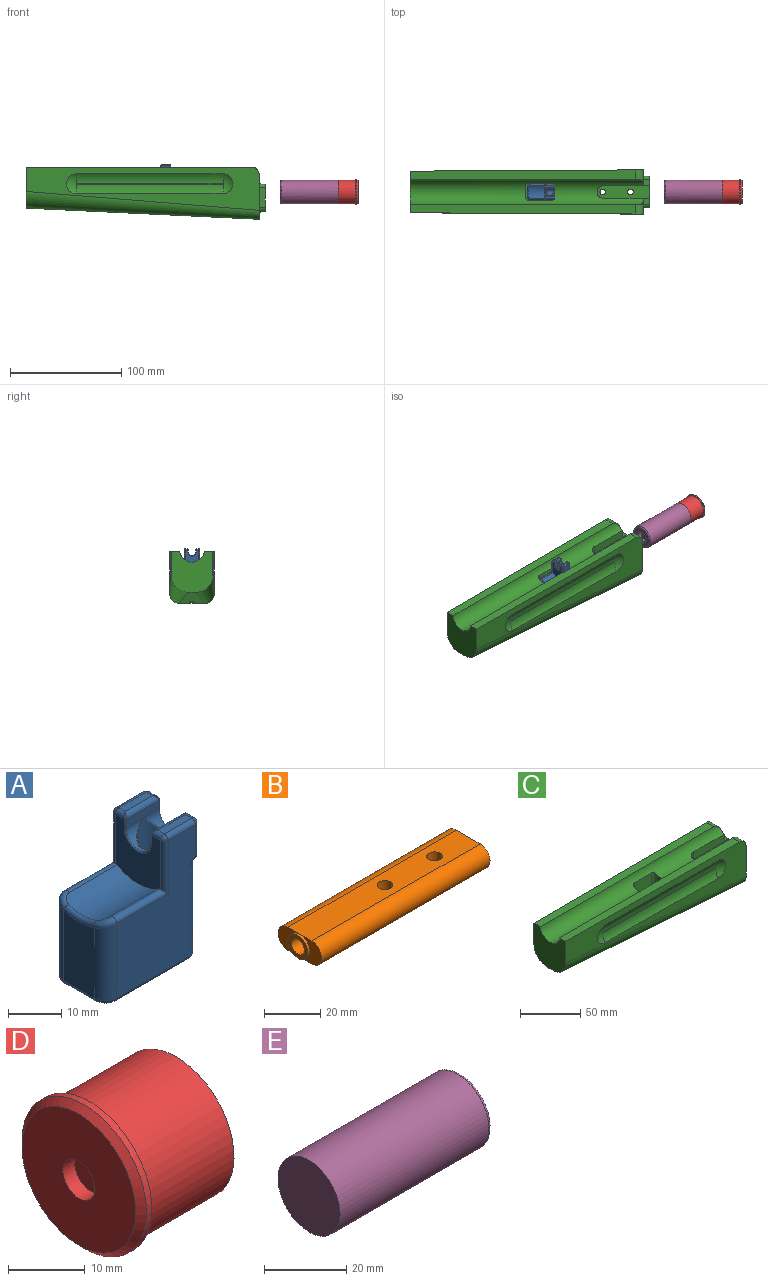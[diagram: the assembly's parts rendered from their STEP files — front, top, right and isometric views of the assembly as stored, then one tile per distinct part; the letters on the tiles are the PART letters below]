
ASSEMBLY  parts=5 mates=4
PART A: 77 faces, bbox 26.7x15.8x31.6 mm
  f0: plane 1.55x0.92mm, normal (1,0,0), area 0.6mm2, adj f1,f75,f76
  f1: cylinder r=6.5mm len=12.57mm, axis (1,0,0), area 12.9mm2, adj f0,f2,f3,f74,f75,f76
  f2: plane 1.55x0.92mm, normal (1,0,0), area 0.6mm2, adj f1,f3,f75
  f3: cylinder r=3mm len=21.61mm, axis (0,0,-1), area 83.5mm2, adj f1,f2,f4,f5,f69,f70,f71,f72
  f4: cylinder r=6.5mm len=12.57mm, axis (1,0,0), area 12.9mm2, adj f3,f5,f74,f76
  f5: plane 18.42x12.1mm, normal (1,0,0), area 136.6mm2, adj f3,f4,f6,f60,f61,f62,f63,f64
  f6: bspline ~2.27x1.53mm, area 0.7mm2, adj f5,f7,f60
  f7: torus R=4mm, axis (0,0,-1), area 2.1mm2, adj f6,f8,f59,f76
  f8: bspline ~2.77x1.82mm, area 0.7mm2, adj f7,f9,f11
  f9: bspline ~1.4x1.29mm, area 0.5mm2, adj f8,f10,f11,f59
  f10: sphere r=1mm, area 0.6mm2, adj f9,f60,f61
  f11: plane 29.5x21mm, normal (0,-1,0), area 407.5mm2, adj f8,f9,f12,f54,f55,f56,f57,f61
  f12: cylinder r=1mm len=19mm, axis (-1,0,0), area 29.8mm2, adj f11,f13,f14,f53
  f13: torus R=2mm, axis (0,0,-1), area 6.5mm2, adj f12,f14,f75,f76
  f14: plane 23x12.1mm, normal (0,0,-1), area 274.9mm2, adj f12,f13,f15,f51,f52,f53,f73,f75
  f15: cylinder r=1mm len=8.1mm, axis (0,1,0), area 12.7mm2, adj f14,f16,f52,f53
  f16: plane 16.26x8.1mm, normal (-1,0,0), area 127.8mm2, adj f15,f17,f50,f54
  f17: cylinder r=3mm len=17.19mm, axis (0,0,-1), area 78.8mm2, adj f16,f18,f52,f72
  f18: bspline ~3.94x3.84mm, area 8.1mm2, adj f17,f19,f48,f50
  f19: cylinder r=1mm len=13.7mm, axis (-1,0,0), area 27.5mm2, adj f18,f20,f47,f48,f72
  f20: cylinder r=1mm len=12.31mm, axis (0,0,-1), area 18.5mm2, adj f19,f21,f47,f72
  f21: sphere r=1mm, area 2.1mm2, adj f20,f22,f45
  f22: cylinder r=1mm len=2.4mm, axis (0,1,0), area 3.2mm2, adj f21,f23,f44,f47
  f23: plane 7.3x1.7mm, normal (0,0,1), area 12.4mm2, adj f22,f24,f45,f66
  f24: cylinder r=1mm len=8.7mm, axis (-1,0,0), area 12.6mm2, adj f23,f25,f43,f44
  f25: plane 8.7x2mm, normal (0,-1,0), area 17.4mm2, adj f24,f26,f41,f42,f65
  f26: cylinder r=3.35mm len=6.7mm, axis (-1,0,0), area 21.3mm2, adj f25,f27,f32,f64
  f27: bspline ~6.7x3.65mm, area 0.6mm2, adj f26,f28
  f28: cylinder r=3.35mm len=16.85mm, axis (0,0,1), area 305.8mm2, adj f27,f29,f30,f31
  f29: bspline ~5.8x3.65mm, area 1.2mm2, adj f28,f41
  f30: bspline ~2.9x2.9mm, area 0.1mm2, adj f28,f41
  f31: torus R=4.65mm, axis (0,1,0), area 132mm2, adj f28,f74
  f32: plane 8.7x2mm, normal (0,1,0), area 17.4mm2, adj f26,f33,f39,f41,f63
  f33: cylinder r=1mm len=8.7mm, axis (-1,0,0), area 12.6mm2, adj f32,f34,f37,f38
  f34: plane 7.3x1.7mm, normal (0,0,1), area 12.4mm2, adj f33,f35,f57,f62
  f35: cylinder r=1mm len=2.4mm, axis (0,1,0), area 3.2mm2, adj f34,f36,f37,f47
  f36: sphere r=1mm, area 1.6mm2, adj f35,f56,f57
  f37: bspline ~1.17x1mm, area 0.3mm2, adj f33,f35,f39
  f38: bspline ~1.04x1mm, area 0.3mm2, adj f33,f62,f63
  f39: cylinder r=0.3mm len=2mm, axis (0,0,-1), area 0.9mm2, adj f32,f37,f40,f47
  f40: torus R=3.65mm, axis (-1,0,0), area 5.1mm2, adj f39,f41,f42,f47
  f41: cylinder r=3.35mm len=6.7mm, axis (-1,0,0), area 21.3mm2, adj f25,f29,f30,f32,f40
  f42: cylinder r=0.3mm len=2mm, axis (0,0,1), area 0.9mm2, adj f25,f40,f44,f47
  f43: bspline ~1.04x1mm, area 0.3mm2, adj f24,f65,f66
  f44: bspline ~1.17x1mm, area 0.3mm2, adj f22,f24,f42
  f45: cylinder r=1mm len=7.3mm, axis (-1,0,0), area 11.5mm2, adj f21,f23,f46,f72
  f46: sphere r=1mm, area 1mm2, adj f45,f66,f67
  f47: plane 12.95x12.1mm, normal (-1,0,0), area 114.1mm2, adj f19,f20,f22,f35,f39,f40,f42,f48
  f48: cylinder r=10.95mm len=14.7mm, axis (-1,0,0), area 166.8mm2, adj f18,f19,f47,f49,f50,f55
  f49: bspline ~3.94x3.84mm, area 8.1mm2, adj f48,f50,f54,f55
  f50: torus R=11.95mm, axis (-1,0,0), area 12.3mm2, adj f16,f18,f48,f49
  f51: cylinder r=1mm len=19mm, axis (1,0,0), area 29.8mm2, adj f14,f52,f72,f73
  f52: torus R=2mm, axis (0,0,-1), area 6.5mm2, adj f14,f15,f17,f51
  f53: torus R=2mm, axis (0,0,-1), area 6.5mm2, adj f12,f14,f15,f54
  f54: cylinder r=3mm len=17.19mm, axis (0,0,-1), area 78.8mm2, adj f11,f16,f49,f53
  f55: cylinder r=1mm len=13.7mm, axis (-1,0,0), area 27.5mm2, adj f11,f47,f48,f49,f56
  f56: cylinder r=1mm len=12.31mm, axis (0,0,1), area 18.5mm2, adj f11,f36,f47,f55
  f57: cylinder r=1mm len=7.3mm, axis (1,0,0), area 11.5mm2, adj f11,f34,f36,f58
  f58: sphere r=1mm, area 1.6mm2, adj f57,f61,f62
  f59: cone r=3mm half-angle=45deg, axis (0,0,1), area 0.1mm2, adj f7,f9,f60
  f60: bspline ~1.72x1.44mm, area 0.5mm2, adj f5,f6,f10,f59
  f61: cylinder r=1mm len=7.06mm, axis (0,0,-1), area 11.1mm2, adj f5,f10,f11,f58
  f62: cylinder r=1mm len=2.4mm, axis (0,1,0), area 3.2mm2, adj f5,f34,f38,f58
  f63: cylinder r=0.3mm len=2mm, axis (0,0,1), area 0.9mm2, adj f5,f32,f38,f64
  f64: torus R=3.65mm, axis (1,0,0), area 5.1mm2, adj f5,f26,f63,f65
  f65: cylinder r=0.3mm len=2mm, axis (0,0,-1), area 0.9mm2, adj f5,f25,f43,f64
  f66: cylinder r=1mm len=2.4mm, axis (0,1,0), area 3.2mm2, adj f5,f23,f43,f46
  f67: cylinder r=1mm len=7.06mm, axis (0,0,1), area 11.1mm2, adj f5,f46,f68,f72
  f68: sphere r=1mm, area 0.6mm2, adj f67,f69,f71
  f69: bspline ~3.13x1.72mm, area 1.6mm2, adj f3,f5,f68,f70
  f70: cone r=3mm half-angle=45deg, axis (0,0,1), area 0.7mm2, adj f3,f69,f71
  f71: bspline ~3x1.66mm, area 1.6mm2, adj f3,f68,f70,f72
  f72: plane 29.5x21mm, normal (0,1,0), area 407.1mm2, adj f3,f17,f19,f20,f45,f51,f67,f71
  f73: torus R=2mm, axis (0,0,-1), area 6.5mm2, adj f3,f14,f51,f75
  f74: plane 13.08x12.65mm, normal (1,0,0), area 94.9mm2, adj f1,f3,f4,f31,f76
  f75: cylinder r=1mm len=8.1mm, axis (0,1,0), area 11mm2, adj f0,f1,f2,f13,f14,f73
  f76: cylinder r=3mm len=20.79mm, axis (0,0,-1), area 80.9mm2, adj f0,f1,f4,f5,f7,f11,f13,f74
PART B: 20 faces, bbox 86x22x10 mm
  f0: plane 85x12mm, normal (0,0,1), area 972.5mm2, adj f2,f3,f5,f6,f7,f18,f19
  f1: plane 85x12mm, normal (0,0,-1), area 972.5mm2, adj f2,f3,f5,f6,f7,f18,f19
  f2: cylinder r=5mm len=85mm, axis (1,0,0), area 1335.2mm2, adj f0,f1,f5,f19
  f3: cylinder r=5mm len=85mm, axis (1,0,0), area 1335.2mm2, adj f0,f1,f5,f18
  f4: plane 10x10mm, normal (-1,0,0), area 45.4mm2, adj f8,f17
  f5: plane 22x10mm, normal (1,0,0), area 165.4mm2, adj f0,f1,f2,f3,f16
  f6: cylinder r=2.75mm len=10mm, axis (0,0,1), area 172.8mm2, adj f0,f1
  f7: cylinder r=2.75mm len=10mm, axis (0,0,1), area 172.8mm2, adj f0,f1
  f8: cylinder r=3.25mm len=9.31mm, axis (1,0,0), area 190.1mm2, adj f4,f9
  f9: torus R=6mm, axis (0,0,-1), area 28.1mm2, adj f8,f10
  f10: cylinder r=3.25mm len=30.13mm, axis (0.97,-0.23,0), area 600.9mm2, adj f9,f11
  f11: torus R=6mm, axis (0,0,1), area 28.1mm2, adj f10,f12
  f12: cylinder r=3.25mm len=29.44mm, axis (1,0,0), area 601.1mm2, adj f11,f13
  f13: torus R=6mm, axis (0,0,1), area 74.1mm2, adj f12,f14
  f14: cylinder r=3.25mm len=10.74mm, axis (0.82,0.57,0), area 175mm2, adj f13,f15
  f15: torus R=6mm, axis (0,0,-1), area 74.1mm2, adj f14,f16
  f16: cylinder r=3.25mm len=6.5mm, axis (1,0,0), area 40.8mm2, adj f5,f15
  f17: cylinder r=5mm len=10mm, axis (-1,0,0), area 31.4mm2, adj f4,f18,f19
  f18: plane 11x10mm, normal (-1,0,0), area 60mm2, adj f0,f1,f3,f17
  f19: plane 11x10mm, normal (-1,0,0), area 60mm2, adj f0,f1,f2,f17
PART C: 58 faces, bbox 216.8x40.9x48.1 mm
  f0: cylinder r=2.5mm len=5mm, axis (0,0,1), area 23.6mm2, adj f39,f46
  f1: cylinder r=2.5mm len=5mm, axis (0,0,1), area 23.6mm2, adj f39,f46
  f2: plane 9.4x8.51mm, normal (-1,0,0), area 73.6mm2, adj f4,f46,f52,f53
  f3: plane 9.4x2mm, normal (-1,0,0), area 18.8mm2, adj f45,f47,f54,f57
  f4: cylinder r=11.4mm len=210mm, axis (1,0,0), area 5991.7mm2, adj f2,f7,f8,f9,f19,f20,f25,f36
  f5: plane 5.66x5.5mm, normal (0.09,0,1), area 29.9mm2, adj f6,f7,f15,f36
  f6: plane 28.12x24.82mm, normal (1,0,0), area 469.1mm2, adj f5,f11,f12,f13,f14,f15,f16,f17
  f7: plane 41.15x40.95mm, normal (1,0,0), area 744.5mm2, adj f4,f5,f9,f10,f11,f12,f13,f14
  f8: plane 203x8.55mm, normal (0,0,1), area 1622.4mm2, adj f4,f10,f19,f25
  f9: cylinder r=7mm len=12.19mm, axis (0,1,0), area 103.9mm2, adj f4,f7,f20,f21
  f10: plane 210.02x39.02mm, normal (-0.01,-1,0), area 3764.1mm2, adj f7,f8,f19,f24,f25,f27,f28,f29
  f11: plane 20.83x5.5mm, normal (0.09,0,-1), area 112.3mm2, adj f6,f7,f17,f18
  f12: plane 18.53x5.5mm, normal (0.09,1,0), area 99.6mm2, adj f6,f7,f15,f17
  f13: plane 5.66x5.5mm, normal (0.09,0,1), area 29.9mm2, adj f6,f7,f16,f38
  f14: plane 18.53x5.5mm, normal (0.09,-1,0), area 99.6mm2, adj f6,f7,f16,f18
  f15: cylinder r=3mm len=5.61mm, axis (-0.99,0.09,0.09), area 26mm2, adj f5,f6,f7,f12
  f16: cylinder r=3mm len=5.61mm, axis (-0.99,-0.09,0.09), area 26mm2, adj f6,f7,f13,f14
  f17: cylinder r=4mm len=5.64mm, axis (-0.99,0.09,-0.09), area 34.7mm2, adj f6,f7,f11,f12
  f18: cylinder r=4mm len=5.64mm, axis (-0.99,-0.09,-0.09), area 34.7mm2, adj f6,f7,f11,f14
  f19: plane 37.5x37mm, normal (-1,0,0), area 1118.6mm2, adj f4,f8,f10,f20,f21,f22,f23,f24
  f20: plane 203x8.55mm, normal (0,0,1), area 1622.4mm2, adj f4,f9,f19,f21
  f21: plane 210.02x39.02mm, normal (-0.01,1,0), area 3764.1mm2, adj f7,f9,f19,f20,f22,f32,f33,f34
  f22: bspline ~210x47mm, area 3795mm2, adj f7,f19,f21,f23
  f23: plane 210.48x24.28mm, normal (-0.05,0,-1), area 3250.9mm2, adj f7,f19,f22,f24,f40,f41
  f24: bspline ~210x34.51mm, area 3795mm2, adj f7,f10,f19,f23
  f25: cylinder r=7mm len=12.19mm, axis (0,1,0), area 103.9mm2, adj f4,f7,f8,f10
  f26: plane 132.54x0.73mm, normal (-0.01,-1,0), area 72.3mm2, adj f27,f28,f29,f30
  f27: torus R=0.27mm, axis (0.01,1,0), area 139.9mm2, adj f10,f26,f28,f29
  f28: cylinder r=15mm len=132.01mm, axis (-1,0.01,0), area 1229.5mm2, adj f10,f26,f27,f30
  f29: cylinder r=15mm len=132.01mm, axis (-1,0.01,0), area 1229.5mm2, adj f10,f26,f27,f30
  f30: torus R=0.27mm, axis (0.01,1,0), area 139.9mm2, adj f10,f26,f28,f29
  f31: plane 132.54x0.73mm, normal (-0.01,1,0), area 72.3mm2, adj f32,f33,f34,f35
  f32: cylinder r=15mm len=132.01mm, axis (1,0.01,0), area 1229.5mm2, adj f21,f31,f33,f34
  f33: torus R=0.27mm, axis (0.01,-1,0), area 139.9mm2, adj f21,f31,f32,f35
  f34: torus R=0.27mm, axis (0.01,-1,0), area 139.9mm2, adj f21,f31,f32,f35
  f35: cylinder r=15mm len=132.01mm, axis (1,0.01,0), area 1229.5mm2, adj f21,f31,f33,f34
  f36: plane 41.25x7.56mm, normal (0,-1,0), area 273.8mm2, adj f4,f5,f6,f7,f37,f39
  f37: cylinder r=5.75mm len=11.5mm, axis (0,0,1), area 122.2mm2, adj f4,f36,f38,f39
  f38: plane 41.25x7.56mm, normal (0,1,0), area 273.8mm2, adj f4,f6,f7,f13,f37,f39
  f39: plane 47x11.5mm, normal (0,0,1), area 487mm2, adj f0,f1,f6,f36,f37,f38
  f40: cylinder r=2.5mm len=18.83mm, axis (0,0,1), area 295.8mm2, adj f23,f47
  f41: cylinder r=2.5mm len=17.64mm, axis (0,0,1), area 277.1mm2, adj f23,f47
  f42: plane 23.2x22.49mm, normal (0,-1,0), area 482.6mm2, adj f4,f45,f48,f51,f52,f54,f55
  f43: plane 20.51x9.4mm, normal (1,0,0), area 186.4mm2, adj f4,f45,f55,f56
  f44: plane 23.2x22.49mm, normal (0,1,0), area 482.6mm2, adj f4,f45,f49,f50,f53,f56,f57
  f45: plane 26.2x15.4mm, normal (0,0,1), area 395.8mm2, adj f3,f42,f43,f44,f54,f55,f56,f57
  f46: plane 85.9x12mm, normal (0,0,-1), area 988.2mm2, adj f0,f1,f2,f6,f50,f51,f52,f53
  f47: plane 85.9x12mm, normal (0,0,1), area 988.2mm2, adj f3,f6,f40,f41,f50,f51,f54,f57
  f48: plane 9.4x3.3mm, normal (1,0,0), area 22.6mm2, adj f42,f51
  f49: plane 9.4x3.3mm, normal (1,0,0), area 22.6mm2, adj f44,f50
  f50: cylinder r=5mm len=88.6mm, axis (1,0,0), area 1350.3mm2, adj f6,f44,f46,f47,f49,f53,f57
  f51: cylinder r=5mm len=88.6mm, axis (1,0,0), area 1350.3mm2, adj f6,f42,f46,f47,f48,f52,f54
  f52: cylinder r=3mm len=10.79mm, axis (0,0,1), area 45.3mm2, adj f2,f4,f42,f46,f51
  f53: cylinder r=3mm len=10.79mm, axis (0,0,-1), area 45.3mm2, adj f2,f4,f44,f46,f50
  f54: cylinder r=3mm len=3mm, axis (0,0,1), area 9.9mm2, adj f3,f42,f45,f47,f51
  f55: cylinder r=3mm len=22.49mm, axis (0,0,-1), area 101.3mm2, adj f4,f42,f43,f45
  f56: cylinder r=3mm len=22.49mm, axis (0,0,1), area 101.3mm2, adj f4,f43,f44,f45
  f57: cylinder r=3mm len=3mm, axis (0,0,-1), area 9.9mm2, adj f3,f44,f45,f47,f50
PART D: 8 faces, bbox 18x23x23 mm
  f0: cylinder r=10.65mm len=21.3mm, axis (-1,0,0), area 1070.7mm2, adj f1,f6
  f1: plane 23x23mm, normal (1,0,0), area 59.1mm2, adj f0,f2
  f2: cylinder r=11.5mm len=23mm, axis (-1,0,0), area 72.3mm2, adj f1,f7
  f3: plane 21x21mm, normal (-1,0,0), area 319mm2, adj f4,f7
  f4: cylinder r=2.95mm len=5.9mm, axis (-1,0,0), area 40.8mm2, adj f3,f5
  f5: plane 5.9x5.9mm, normal (-1,0,0), area 27.3mm2, adj f4
  f6: plane 21.3x21.3mm, normal (1,0,0), area 356.3mm2, adj f0
  f7: cone r=10.5mm half-angle=45deg, axis (1,0,0), area 97.7mm2, adj f2,f3
PART E: 7 faces, bbox 52x23.1x23.1 mm
  f0: cylinder r=10.65mm len=51mm, axis (-1,0,0), area 3412.7mm2, adj f1,f6
  f1: plane 21.3x21.3mm, normal (-1,0,0), area 356.3mm2, adj f0
  f2: plane 9.7x9.7mm, normal (1,0,0), area 73.9mm2, adj f3
  f3: cylinder r=4.85mm len=9.7mm, axis (-1,0,0), area 103.6mm2, adj f2,f5
  f4: plane 19.3x19.3mm, normal (1,0,0), area 185mm2, adj f5,f6
  f5: torus R=5.85mm, axis (1,0,0), area 51.5mm2, adj f3,f4
  f6: torus R=9.65mm, axis (1,0,0), area 101.5mm2, adj f0,f4
PLACE A t=(125.85,0,-2.32)mm
PLACE B t=(215.5,0,-23.9)mm
PLACE C t=(210,0,-29.25)mm
PLACE D rot(axis=(0,-0.91,-0.41),180deg) t=(298.91,0,-23.9)mm
PLACE E rot(axis=(0,-0.91,-0.41),180deg) t=(298.91,0,-23.9)mm
MATE fastened A.f74 <-> B.f17  axis (1,0,0) through (129.5,0,-23.9)mm
MATE fastened B.f6 <-> C.f1  axis (0,0,1) through (173.5,0,-18.9)mm
MATE fastened D.f0 <-> E.f0  axis (-1,0,0) through (280.91,0,-23.9)mm
MATE cylindrical B.f16 <-> E.f0  axis (1,0,0) through (215.5,0,-23.9)mm
